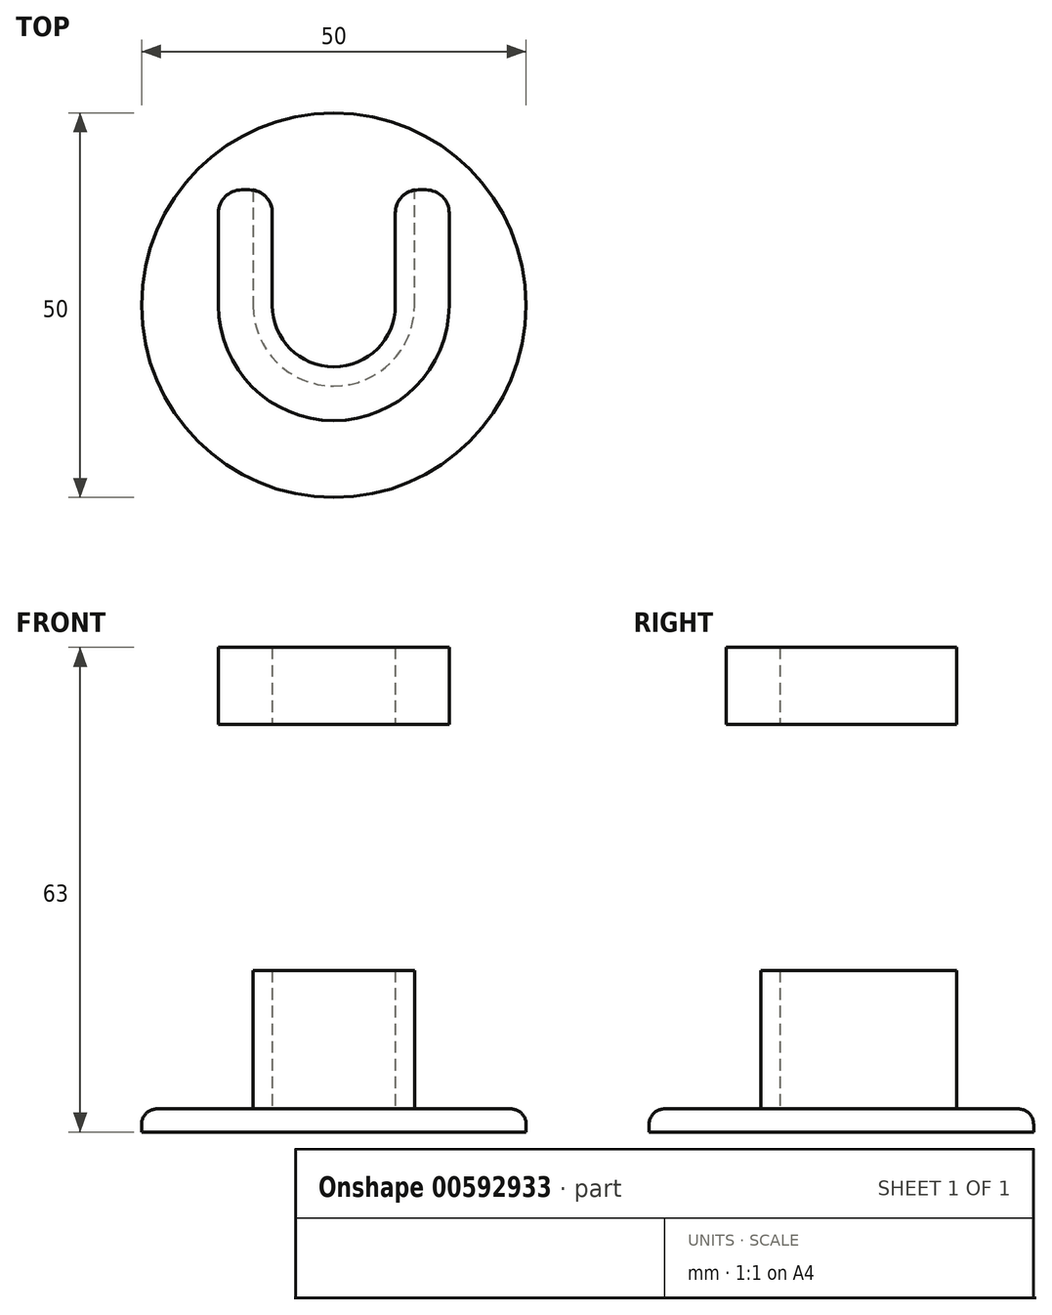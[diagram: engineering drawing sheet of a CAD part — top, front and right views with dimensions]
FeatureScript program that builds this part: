
annotation { "Feature Type Name" : "Feature", "Feature Type Description" : "" }
export const myFeature = defineFeature(function(context is Context, id is Id, definition is map)
    precondition{}
    {
        {
            var Q0;
            Q0=qCreatedBy(makeId("Top.planeOp"),FACE);
            var sketch = newSketch(context, id + "F0", { "sketchPlane" : qUnion([Q0])});
            skCircle(sketch, "E0", {"center": v(0, 0) * mm, "radius": 25 * mm});
            skCircle(sketch, "E1", {"center": v(0, 0) * mm, "radius": 8 * mm});
            skCircle(sketch, "E2", {"center": v(0, 0) * mm, "radius": 10.5 * mm});
            skLineSegment(sketch, "E3", {"start": v(-10.5, 15) * mm, "end": v(-10.5, 0) * mm});
            skLineSegment(sketch, "E4", {"start": v(-20, 15) * mm, "end": v(20, 15) * mm});
            skLineSegment(sketch, "E5", {"start": v(-8, 0) * mm, "end": v(-8, 15) * mm});
            skLineSegment(sketch, "E6", {"start": v(8, 0) * mm, "end": v(8, 15) * mm});
            skLineSegment(sketch, "E7", {"start": v(10.5, 0) * mm, "end": v(10.5, 15) * mm});
            skSolve(sketch);
        }
        {
            var Q0;
            Q0 = qSketchRegion(id + "F0", true);
            var Q1;
            Q1=makeQuery(id+"F0.imprint","IMPRINT",FACE,{"disambiguationData":[TD([[makeQuery(id+"F0.imprint","IMPRINT",EDGE,{"derivedFrom":sQuery(id+"F0.wireOp",EDGE,"E1")}),1.0]])]});
            var Q2;
            Q2=makeQuery(id+"F0.imprint","IMPRINT",FACE,{"disambiguationData":[TD([[makeQuery(id+"F0.imprint","IMPRINT",EDGE,{"derivedFrom":sQuery(id+"F0.wireOp",EDGE,"E1")}),-1.0]])]});
            var Q3;
            {var subQ0=sQuery(id+"F0.wireOp",EDGE,"E2");var subQ1=makeQuery(id+"F0.imprint","IMPRINT",VERTEX,{"disambiguationData":[OD(0.0)],"derivedFrom":subQ0});Q3=makeQuery(id+"F0.imprint","IMPRINT",FACE,{"disambiguationData":[TD([[makeQuery(id+"F0.imprint","IMPRINT",EDGE,{"disambiguationData":[TD([[subQ1,-1.0]])],"derivedFrom":subQ0}),1.0]])]});}
            var Q4;
            {var subQ0=sQuery(id+"F0.wireOp",EDGE,"E3");Q4=makeQuery(id+"F0.imprint","IMPRINT",FACE,{"disambiguationData":[TD([[makeQuery(id+"F0.imprint","IMPRINT",EDGE,{"derivedFrom":subQ0}),1.0]])]});}
            var Q5;
            {var subQ0=sQuery(id+"F0.wireOp",EDGE,"E6");var subQ1=sQuery(id+"F0.wireOp",EDGE,"E2");var subQ2=makeQuery(id+"F0.imprint","INTERSECT",VERTEX,{"derivedFrom":[subQ1,subQ0]});Q5=makeQuery(id+"F0.imprint","IMPRINT",FACE,{"disambiguationData":[TD([[makeQuery(id+"F0.imprint","IMPRINT",EDGE,{"disambiguationData":[TD([[subQ2,-1.0]])],"derivedFrom":subQ1}),-1.0]])]});}
            var Q6;
            {var subQ0=sQuery(id+"F0.wireOp",EDGE,"E7");Q6=makeQuery(id+"F0.imprint","IMPRINT",FACE,{"disambiguationData":[TD([[makeQuery(id+"F0.imprint","IMPRINT",EDGE,{"derivedFrom":subQ0}),1.0]])]});}
            var Q7;
            {var subQ3=sQuery(id+"F0.wireOp",EDGE,"E5");var subQ7=sQuery(id+"F0.wireOp",EDGE,"E1");var subQ8=makeQuery(id+"F0.imprint","INTERSECT",VERTEX,{"derivedFrom":[subQ7,subQ3]});Q7=makeQuery(id+"F0.imprint","IMPRINT",FACE,{"disambiguationData":[TD([[makeQuery(id+"F0.imprint","IMPRINT",EDGE,{"disambiguationData":[TD([[subQ8,-1.0]])],"derivedFrom":subQ7}),-1.0]])]});}
            extrude(context, id + "F1", {"entities" : qUnion([Q0, Q1, Q2, Q3, Q4, Q5, Q6, Q7]), "oppositeDirection" : true, "depth" : 3 * mm, "offsetDistance" : 25 * mm});
        }
        {
            var Q0;
            {var subQ0=sQuery(id+"F0.wireOp",EDGE,"E7");Q0=makeQuery(id+"F0.imprint","IMPRINT",FACE,{"disambiguationData":[TD([[makeQuery(id+"F0.imprint","IMPRINT",EDGE,{"derivedFrom":subQ0}),1.0]])]});}
            var Q1;
            {var subQ3=sQuery(id+"F0.wireOp",EDGE,"E5");var subQ7=sQuery(id+"F0.wireOp",EDGE,"E1");var subQ8=makeQuery(id+"F0.imprint","INTERSECT",VERTEX,{"derivedFrom":[subQ7,subQ3]});Q1=makeQuery(id+"F0.imprint","IMPRINT",FACE,{"disambiguationData":[TD([[makeQuery(id+"F0.imprint","IMPRINT",EDGE,{"disambiguationData":[TD([[subQ8,-1.0]])],"derivedFrom":subQ7}),-1.0]])]});}
            var Q2;
            {var subQ0=sQuery(id+"F0.wireOp",EDGE,"E3");Q2=makeQuery(id+"F0.imprint","IMPRINT",FACE,{"disambiguationData":[TD([[makeQuery(id+"F0.imprint","IMPRINT",EDGE,{"derivedFrom":subQ0}),1.0]])]});}
            extrude(context, id + "F2", {"entities" : qUnion([Q0, Q1, Q2]), "operationType" : NewBodyOperationType.ADD, "depth" : 18 * mm, "offsetDistance" : 25 * mm});
        }
        {
            var Q0;
            Q0=makeQuery(id+"F1.opExtrude","CAP_EDGE",EDGE,{"disambiguationData":[OSD([sQuery(id+"F0.wireOp",EDGE,"E0")])],"isStart":true});
            var Q1;
            Q1=makeQuery(id+"F2.opExtrude","CAP_EDGE",EDGE,{"disambiguationData":[OSD([sQuery(id+"F0.wireOp",EDGE,"E2")])],"isStart":true});
            fillet(context, id + "F3", {"entities" : qUnion([Q0, Q1]), "radius" : 2 * mm, "tangentPropagation" : true, "allowEdgeOverflow" : false});
        }
        {
            var Q0;
            Q0=makeQuery(id+"F2.opExtrude","SWEPT_EDGE",EDGE,{"disambiguationData":[OSD([sQuery(id+"F0.wireOp",EDGE,"E4"),sQuery(id+"F0.wireOp",EDGE,"E5")])]});
            var Q1;
            Q1=makeQuery(id+"F2.opExtrude","SWEPT_EDGE",EDGE,{"disambiguationData":[OSD([sQuery(id+"F0.wireOp",EDGE,"E4"),sQuery(id+"F0.wireOp",EDGE,"E6")])]});
            fillet(context, id + "F4", {"entities" : qUnion([Q0, Q1]), "radius" : 3 * mm, "tangentPropagation" : true, "allowEdgeOverflow" : false});
        }
        {
            var Q0;
            Q0=qCreatedBy(makeId("Top.planeOp"),FACE);
            cPlane(context, id + "F5", {"entities" : qUnion([Q0]), "cplaneType" : CPlaneType.OFFSET, "offset" : 50 * mm, "width" : 150 * mm, "height" : 150 * mm});
        }
        {
            var Q0;
            Q0=qCreatedBy(id+"F5.planeOp",FACE);
            var sketch = newSketch(context, id + "F6", { "sketchPlane" : qUnion([Q0])});
            skCircle(sketch, "E8", {"center": v(0, 0) * mm, "radius": 15 * mm});
            skCircle(sketch, "E9", {"center": v(0, 0) * mm, "radius": 8 * mm});
            skLineSegment(sketch, "E10", {"start": v(-15, 0) * mm, "end": v(-15, 15) * mm});
            skLineSegment(sketch, "E11", {"start": v(-8, 0) * mm, "end": v(-8, 15) * mm});
            skLineSegment(sketch, "E12", {"start": v(8, 0) * mm, "end": v(8, 15) * mm});
            skLineSegment(sketch, "E13", {"start": v(15, 0) * mm, "end": v(15, 15) * mm});
            skLineSegment(sketch, "E14", {"start": v(15, 15) * mm, "end": v(8, 15) * mm});
            skLineSegment(sketch, "E15", {"start": v(-15, 15) * mm, "end": v(-8, 15) * mm});
            skSolve(sketch);
        }
        {
            var Q0;
            {var subQ0=sQuery(id+"F6.wireOp",EDGE,"E10");Q0=makeQuery(id+"F6.imprint","IMPRINT",FACE,{"disambiguationData":[TD([[makeQuery(id+"F6.imprint","IMPRINT",EDGE,{"derivedFrom":subQ0}),-1.0]])]});}
            var Q1;
            {var subQ0=sQuery(id+"F6.wireOp",EDGE,"E8");var subQ2=makeQuery(id+"F6.imprint","INTERSECT",VERTEX,{"derivedFrom":[subQ0,sQuery(id+"F6.wireOp",EDGE,"E13")]});Q1=makeQuery(id+"F6.imprint","IMPRINT",FACE,{"disambiguationData":[TD([[makeQuery(id+"F6.imprint","IMPRINT",EDGE,{"disambiguationData":[TD([[subQ2,-1.0]])],"derivedFrom":subQ0}),1.0]])]});}
            var Q2;
            {var subQ0=sQuery(id+"F6.wireOp",EDGE,"E13");Q2=makeQuery(id+"F6.imprint","IMPRINT",FACE,{"disambiguationData":[TD([[makeQuery(id+"F6.imprint","IMPRINT",EDGE,{"derivedFrom":subQ0}),1.0]])]});}
            extrude(context, id + "F7", {"entities" : qUnion([Q0, Q1, Q2]), "depth" : 10 * mm, "offsetDistance" : 25 * mm});
        }
        {
            var Q0;
            Q0=makeQuery(id+"F7.opExtrude","SWEPT_EDGE",EDGE,{"disambiguationData":[OSD([sQuery(id+"F6.wireOp",EDGE,"E11"),sQuery(id+"F6.wireOp",EDGE,"E15")])]});
            var Q1;
            Q1=makeQuery(id+"F7.opExtrude","SWEPT_EDGE",EDGE,{"disambiguationData":[OSD([sQuery(id+"F6.wireOp",EDGE,"E12"),sQuery(id+"F6.wireOp",EDGE,"E14")])]});
            var Q2;
            Q2=makeQuery(id+"F7.opExtrude","SWEPT_EDGE",EDGE,{"disambiguationData":[OSD([sQuery(id+"F6.wireOp",EDGE,"E10"),sQuery(id+"F6.wireOp",EDGE,"E15")])]});
            var Q3;
            Q3=makeQuery(id+"F7.opExtrude","SWEPT_EDGE",EDGE,{"disambiguationData":[OSD([sQuery(id+"F6.wireOp",EDGE,"E13"),sQuery(id+"F6.wireOp",EDGE,"E14")])]});
            fillet(context, id + "F8", {"entities" : qUnion([Q0, Q1, Q2, Q3]), "radius" : 3 * mm, "tangentPropagation" : true, "allowEdgeOverflow" : false});
        }
    });
